# Revit family: L-industry 115
name_source: partatom
category: Осветительные приборы
revit_build: Autodesk Revit 2017 (Build: 20160225_1515(x64)
units: mm (PartAtom-declared; Revit-internal decimal feet)

## family parameters
Всегда вертикально = Да
Заголовок OmniClass = Luminaries for Internal Lighting
Источник света = Да
Номер OmniClass = 23.80.70.11
Общий = Нет
Основа = Потолок
При загрузке вырезать с полостями = Нет
Размер круглого соединителя = Использовать диаметр
Тип детали = Нормальный
Точка расчета площади = Нет

## types (8) — shared parameters
Видимая форма излучения при визуализации = Нет
Изготовитель = LEDEL
Классификация нагрузок = Освещение
Комментарии к типоразмеру = Промышленные
Описание = Светильник c аварийным блоком освещения L-office 32 Em Premium предназначен для установки в помещениях торгово-офисного и административного назначения.
Полная установленная мощность = 94 В·А
Светофильтр = 16777215
Смещение цветовой температуры при затухании лампы = <Нет>
Угол наклона = 90.00°

## per-type parameters (varying)
| type | Артикул | Длина подвеса светильника | Излучение по диаметру окружности | Расстояние от потолка до светильника | Файл фотометрической сетки |
| L-industry 115 4.0К К15 | 515111102741300 | 1008 мм | 136 мм | 1458 мм | L-industry 115-94-K15-4.0K-01.ies |
| L-industry 115 5.0К Д | 407013 | 1008 мм | 136 мм | 1458 мм | L-industry 115-94-D-5.0K-01.ies |
| L-industry 115 5.0К К15 | 407012 | 1008 мм | 136 мм | 1458 мм | L-industry 115-94-K15-5.0K-01.ies |
| L-industry 115 4.0К Д | 515111100741300 | 1008 мм | 136 мм | 1458 мм | L-industry 115-94-D-4.0K-01.ies |
| L-industry 115 4.0К Г30 | 515111104741300 | 500 мм | 134 мм | 950 мм | L-industry 115-94-G30-4.0K-01.ies |
| L-industry 115 5.0К Г30 | 407011 | 1008 мм | 136 мм | 1458 мм | L-industry 115-94-G30-5.0K-01.ies |
| L-industry 115 4.0К Г60 | 515111106741300
515111106741300 | 1008 мм | 136 мм | 1458 мм | L-industry 115-94-G60-4.0K-01.ies |
| L-industry 115 5.0К Г60 | 407010
407010 | 1008 мм | 136 мм | 1458 мм | L-industry 115-94-G60-5.0K-01.ies |

## geometry (parser evidence)
native form markers: Sweep x1
no freeform markers — native parametric forms only
